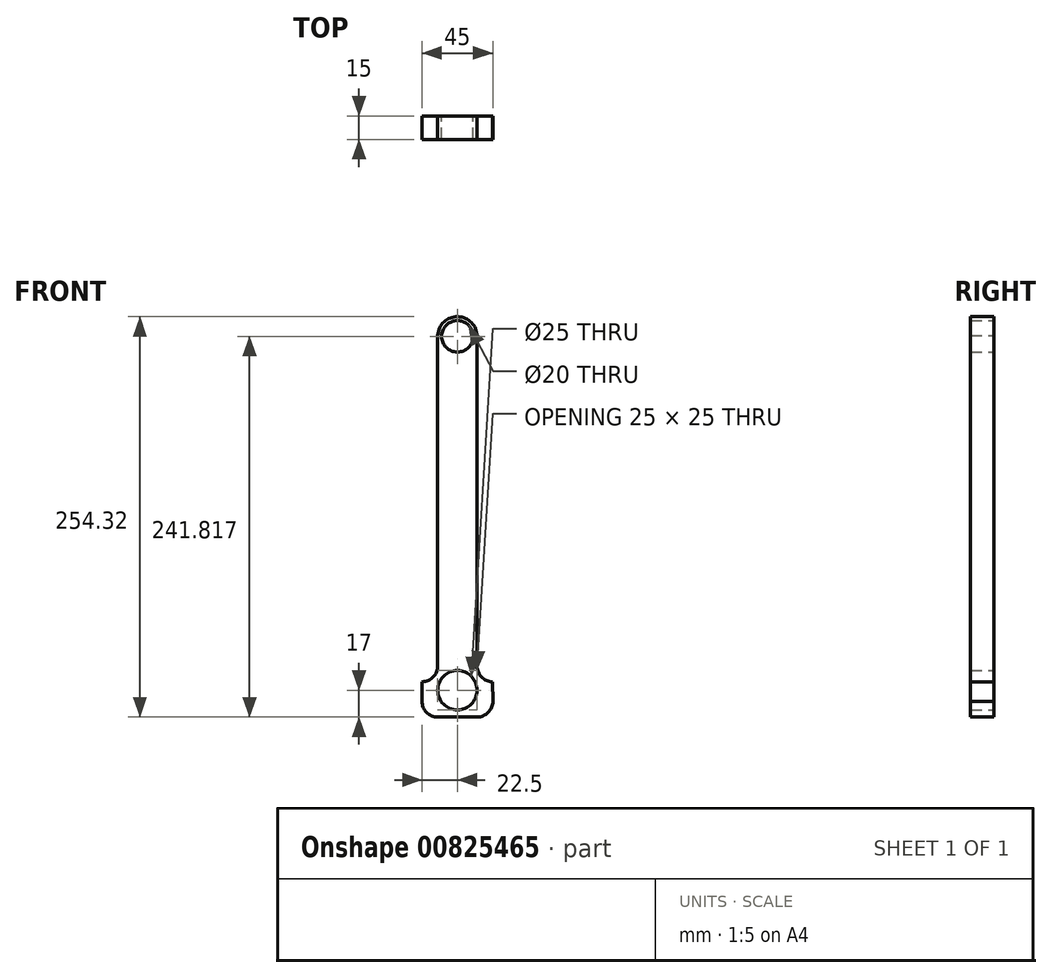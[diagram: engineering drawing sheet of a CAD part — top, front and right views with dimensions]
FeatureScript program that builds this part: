
annotation { "Feature Type Name" : "Feature", "Feature Type Description" : "" }
export const myFeature = defineFeature(function(context is Context, id is Id, definition is map)
    precondition{}
    {
        {
            var Q0;
            Q0=qCreatedBy(makeId("Front.planeOp"),FACE);
            var sketch = newSketch(context, id + "F0", { "sketchPlane" : qUnion([Q0])});
            skPoint(sketch, "E0", {"position": v(0, 224.82) * mm});
            skPoint(sketch, "E1", {"position": v(0, 0) * mm});
            skCircle(sketch, "E2", {"center": v(0, 224.82) * mm, "radius": 12.5 * mm});
            skCircle(sketch, "E3", {"center": v(0, 0) * mm, "radius": 12.5 * mm});
            skLineSegment(sketch, "E4", {"start": v(-12.49, 225.4) * mm, "end": v(-12.5, 15.4) * mm});
            skLineSegment(sketch, "E5", {"start": v(12.5, 0) * mm, "end": v(12.5, 0) * mm});
            skLineSegment(sketch, "E6.top", {"start": v(-12.5, -17) * mm, "end": v(12.5, -17) * mm});
            skLineSegment(sketch, "E7.trimOffspring", {"start": v(-12.5, 0) * mm, "end": v(-12.5, 0) * mm});
            skLineSegment(sketch, "E8.trimOffspring", {"start": v(12.5, 15.33) * mm, "end": v(12.5, 224.82) * mm});
            skArc(sketch, "E9.filletArc", {"start": v(-22.33, 5.4) * mm, "mid": v(-15.37, 8.4) * mm, "end": v(-12.5, 15.4) * mm});
            skPoint(sketch, "E10.visualSharp", {"position": v(12.5, 90.32) * mm});
            skArc(sketch, "E10.filletArc", {"start": v(12.5, 15.33) * mm, "mid": v(15.37, 8.32) * mm, "end": v(22.33, 5.33) * mm});
            skPoint(sketch, "E11.visualSharp", {"position": v(-22.5, 12.5) * mm});
            skPoint(sketch, "E12.visualSharp", {"position": v(-22.5, -17) * mm});
            skArc(sketch, "E12.filletArc", {"start": v(-22.5, -7) * mm, "mid": v(-19.57, -14.07) * mm, "end": v(-12.5, -17) * mm});
            skPoint(sketch, "E13.visualSharp", {"position": v(22.5, -17) * mm});
            skArc(sketch, "E13.filletArc", {"start": v(12.5, -17) * mm, "mid": v(19.57, -14.07) * mm, "end": v(22.5, -7) * mm});
            skPoint(sketch, "E14.visualSharp", {"position": v(22.5, 12.5) * mm});
            skCircle(sketch, "E15", {"center": v(0, 224.82) * mm, "radius": 10 * mm});
            skLineSegment(sketch, "E16", {"start": v(-22.33, 5.4) * mm, "end": v(-22.5, -7) * mm});
            skLineSegment(sketch, "E17", {"start": v(22.5, -7) * mm, "end": v(22.33, 5.33) * mm});
            skSolve(sketch);
        }
        {
            var Q0;
            {var subQ0=sQuery(id+"F0.wireOp",EDGE,"E5");var subQ1=sQuery(id+"F0.wireOp",EDGE,"E2");var subQ2=makeQuery(id+"F0.imprint","INTERSECT",VERTEX,{"derivedFrom":[subQ1,subQ0]});Q0=makeQuery(id+"F0.imprint","IMPRINT",FACE,{"disambiguationData":[TD([[makeQuery(id+"F0.imprint","IMPRINT",EDGE,{"disambiguationData":[TD([[subQ2,1.0]])],"derivedFrom":subQ1}),-1.0]])]});}
            var Q1;
            Q1=makeQuery(id+"F0.imprint","IMPRINT",FACE,{"disambiguationData":[TD([[makeQuery(id+"F0.imprint","IMPRINT",EDGE,{"derivedFrom":sQuery(id+"F0.wireOp",EDGE,"mSTLdB2U-qB6p-trkz-ORDn-0SVQ7sgYyeDw")}),-1.0]])]});
            var Q2;
            Q2=makeQuery(id+"F0.imprint","IMPRINT",FACE,{"disambiguationData":[TD([[makeQuery(id+"F0.imprint","IMPRINT",EDGE,{"derivedFrom":sQuery(id+"F0.wireOp",EDGE,"U24O8jUd-l9Od-7IED-efZo-MopYym5HXAEv")}),-1.0]])]});
            var Q3;
            Q3=makeQuery(id+"F0.imprint","IMPRINT",FACE,{"disambiguationData":[TD([[makeQuery(id+"F0.imprint","IMPRINT",EDGE,{"derivedFrom":sQuery(id+"F0.wireOp",EDGE,"E15")}),-1.0]])]});
            extrude(context, id + "F1", {"entities" : qUnion([Q0, Q1, Q2, Q3]), "depth" : 15 * mm, "offsetDistance" : 25 * mm});
        }
    });
